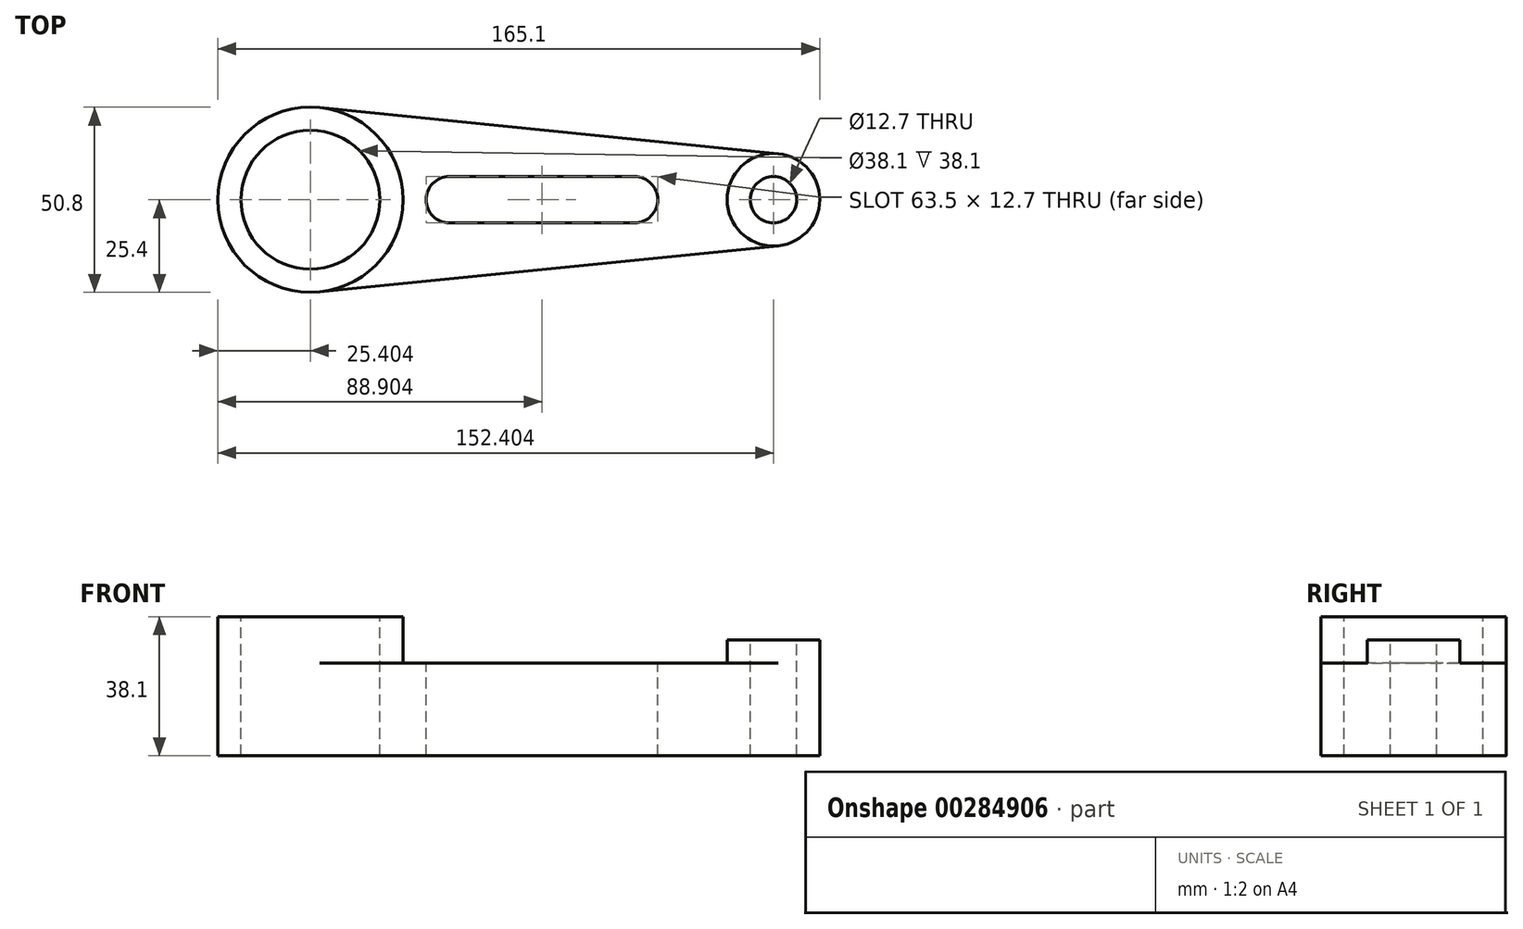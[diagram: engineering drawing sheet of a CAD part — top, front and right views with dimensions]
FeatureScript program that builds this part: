
annotation { "Feature Type Name" : "Feature", "Feature Type Description" : "" }
export const myFeature = defineFeature(function(context is Context, id is Id, definition is map)
    precondition{}
    {
        {
            var Q0;
            Q0=qCreatedBy(makeId("Top.planeOp"),FACE);
            var sketch = newSketch(context, id + "F0", { "sketchPlane" : qUnion([Q0])});
            skCircle(sketch, "E0", {"center": v(-61.78, 0) * mm, "radius": 19.05 * mm});
            skCircle(sketch, "E1", {"center": v(-61.78, 0) * mm, "radius": 25.4 * mm});
            skCircle(sketch, "E2", {"center": v(65.22, 0) * mm, "radius": 6.35 * mm});
            skCircle(sketch, "E3", {"center": v(65.22, 0) * mm, "radius": 12.7 * mm});
            skLineSegment(sketch, "E4", {"start": v(-59.24, 25.27) * mm, "end": v(66.5, 12.64) * mm});
            skLineSegment(sketch, "E5", {"start": v(-59.24, -25.27) * mm, "end": v(66.5, -12.64) * mm});
            skPoint(sketch, "E6", {"position": v(-23.68, 0) * mm});
            skPoint(sketch, "E7", {"position": v(27.12, 0) * mm});
            skArc(sketch, "E8", {"start": v(-23.68, 6.35) * mm, "mid": v(-30.03, 0) * mm, "end": v(-23.68, -6.35) * mm});
            skArc(sketch, "E9", {"start": v(27.12, -6.35) * mm, "mid": v(33.47, 0) * mm, "end": v(27.12, 6.35) * mm});
            skLineSegment(sketch, "E10", {"start": v(-23.68, 6.35) * mm, "end": v(27.12, 6.35) * mm});
            skLineSegment(sketch, "E11", {"start": v(-23.68, -6.35) * mm, "end": v(27.12, -6.35) * mm});
            skSolve(sketch);
        }
        {
            var Q0;
            Q0=makeQuery(id+"F0.imprint","IMPRINT",FACE,{"disambiguationData":[TD([[makeQuery(id+"F0.imprint","IMPRINT",EDGE,{"derivedFrom":sQuery(id+"F0.wireOp",EDGE,"E0")}),-1.0]])]});
            var Q1;
            {var subQ0=sQuery(id+"F0.wireOp",EDGE,"E4");Q1=makeQuery(id+"F0.imprint","IMPRINT",FACE,{"disambiguationData":[TD([[makeQuery(id+"F0.imprint","IMPRINT",EDGE,{"derivedFrom":subQ0}),-1.0]])]});}
            var Q2;
            Q2=makeQuery(id+"F0.imprint","IMPRINT",FACE,{"disambiguationData":[TD([[makeQuery(id+"F0.imprint","IMPRINT",EDGE,{"derivedFrom":sQuery(id+"F0.wireOp",EDGE,"E2")}),-1.0]])]});
            extrude(context, id + "F1", {"entities" : qUnion([Q0, Q1, Q2]), "oppositeDirection" : true, "depth" : 38.1 * mm});
        }
        {
            var Q0;
            {var subQ0=sQuery(id+"F0.wireOp",EDGE,"E4");Q0=makeQuery(id+"F0.imprint","IMPRINT",FACE,{"disambiguationData":[TD([[makeQuery(id+"F0.imprint","IMPRINT",EDGE,{"derivedFrom":subQ0}),-1.0]])]});}
            extrude(context, id + "F2", {"entities" : qUnion([Q0]), "operationType" : NewBodyOperationType.REMOVE, "oppositeDirection" : true, "depth" : 12.7 * mm});
        }
        {
            var Q0;
            {var subQ0=sQuery(id+"F0.wireOp",EDGE,"E2");var subQ1=sQuery(id+"F0.wireOp",EDGE,"E3");Q0=makeQuery(id+"F2.boolean.opBoolean","SPLIT",FACE,{"disambiguationData":[TD([makeQuery(id+"F1.opExtrude","SWEPT_FACE",FACE,{"disambiguationData":[OSD([subQ0])]})])],"derivedFrom":makeQuery(id+"F1.opExtrude","CAP_FACE",FACE,{"disambiguationData":[OSD([sQuery(id+"F0.wireOp",EDGE,"E0"),sQuery(id+"F0.wireOp",EDGE,"E1"),subQ0,subQ1,sQuery(id+"F0.wireOp",EDGE,"E4"),sQuery(id+"F0.wireOp",EDGE,"E5"),sQuery(id+"F0.wireOp",EDGE,"E8"),sQuery(id+"F0.wireOp",EDGE,"E9"),sQuery(id+"F0.wireOp",EDGE,"E10"),sQuery(id+"F0.wireOp",EDGE,"E11")])],"isStart":true})});}
            extrude(context, id + "F3", {"entities" : qUnion([Q0]), "operationType" : NewBodyOperationType.REMOVE, "oppositeDirection" : true, "depth" : 6.35 * mm});
        }
    });
